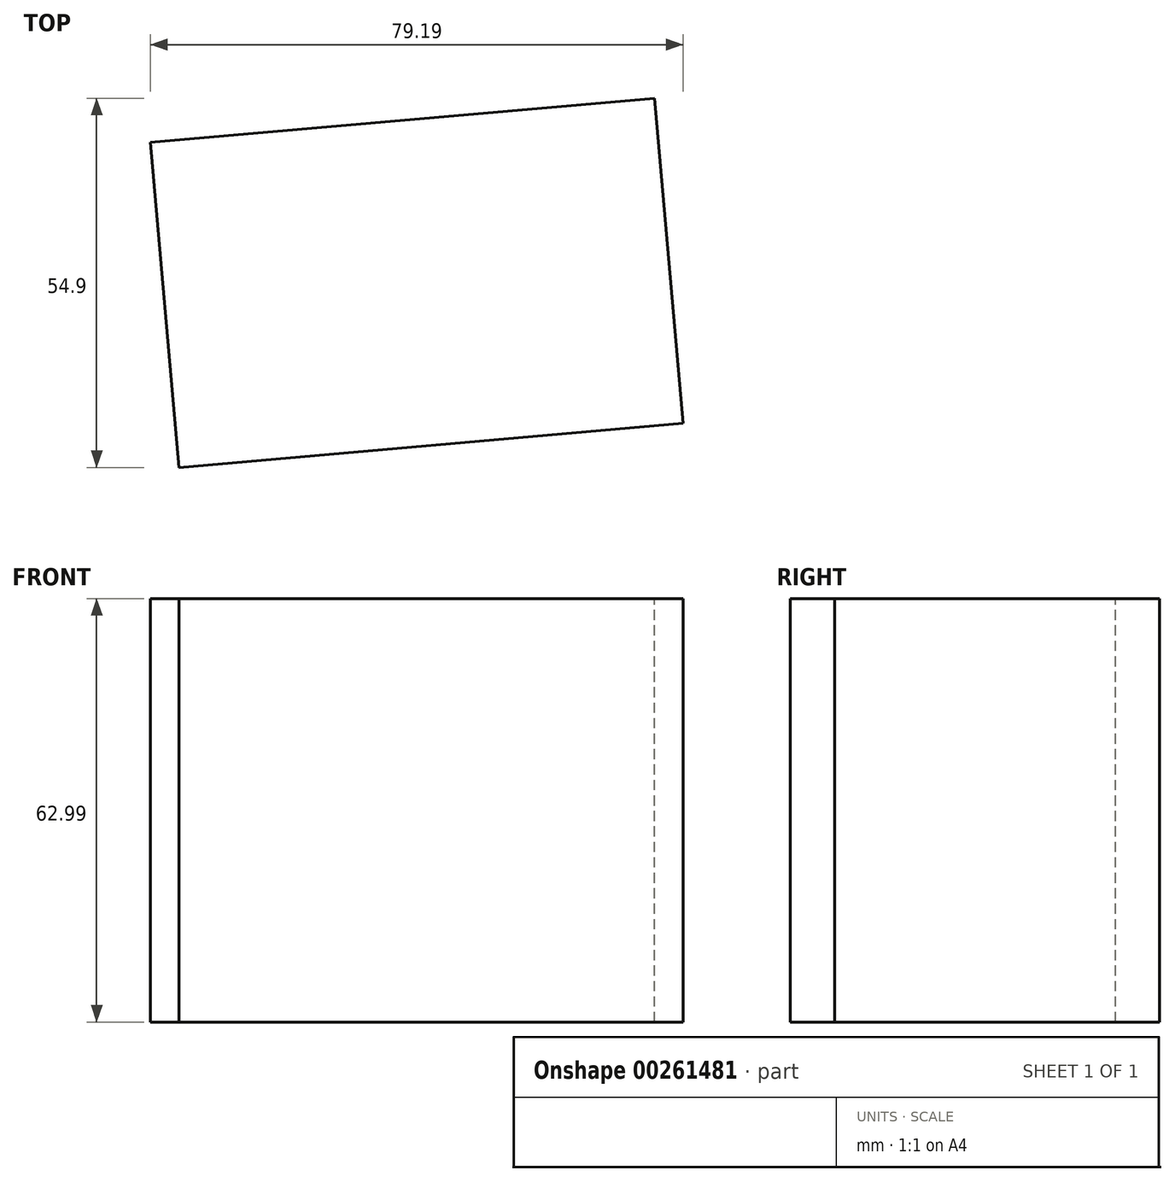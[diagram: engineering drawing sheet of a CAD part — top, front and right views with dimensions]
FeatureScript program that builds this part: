
annotation { "Feature Type Name" : "Feature", "Feature Type Description" : "" }
export const myFeature = defineFeature(function(context is Context, id is Id, definition is map)
    precondition{}
    {
        {
            var Q0;
            Q0=qCreatedBy(makeId("Top.planeOp"),FACE);
            var sketch = newSketch(context, id + "F0", { "sketchPlane" : qUnion([Q0])});
            skLineSegment(sketch, "E0.bottom", {"start": v(-41.34, -12.73) * mm, "end": v(33.91, -12.73) * mm});
            skLineSegment(sketch, "E0.top", {"start": v(-41.34, 35.8) * mm, "end": v(33.91, 35.8) * mm});
            skLineSegment(sketch, "E0.left", {"start": v(-41.34, -12.73) * mm, "end": v(-41.34, 35.8) * mm});
            skLineSegment(sketch, "E0.right", {"start": v(33.91, -12.73) * mm, "end": v(33.91, 35.8) * mm});
            skSolve(sketch);
        }
        {
            var Q0;
            Q0 = qSketchRegion(id + "F0", true);
            extrude(context, id + "F1", {"entities" : qUnion([Q0]), "depth" : 63 * mm});
        }
        {
            var Q0;
            Q0=makeQuery(id+"F1.opExtrude","SWEPT_BODY",BODY,{"disambiguationData":[OSD([sQuery(id+"F0.wireOp",EDGE,"E0.bottom"),sQuery(id+"F0.wireOp",EDGE,"E0.top"),sQuery(id+"F0.wireOp",EDGE,"E0.left"),sQuery(id+"F0.wireOp",EDGE,"E0.right")])]});
            var Q1;
            Q1=makeQuery(id+"F1.opExtrude","SWEPT_EDGE",EDGE,{"disambiguationData":[OSD([sQuery(id+"F0.wireOp",EDGE,"E0.top"),sQuery(id+"F0.wireOp",EDGE,"E0.right")])]});
            transform(context, id + "F2", {"entities" : qUnion([Q0]), "transformType" : TransformType.ROTATION, "transformAxis" : qUnion([Q1]), "angle" : 175 * degree, "makeCopy" : false});
        }
        {
            var Q0;
            Q0=makeQuery(id+"F1.opExtrude","SWEPT_BODY",BODY,{"disambiguationData":[OSD([sQuery(id+"F0.wireOp",EDGE,"E0.bottom"),sQuery(id+"F0.wireOp",EDGE,"E0.top"),sQuery(id+"F0.wireOp",EDGE,"E0.left"),sQuery(id+"F0.wireOp",EDGE,"E0.right")])]});
            var Q1;
            Q1=makeQuery(id+"F1.opExtrude","CAP_EDGE",EDGE,{"disambiguationData":[OSD([sQuery(id+"F0.wireOp",EDGE,"E0.right")])],"isStart":true});
            transform(context, id + "F3", {"entities" : qUnion([Q0]), "transformType" : TransformType.ROTATION, "transformAxis" : qUnion([Q1]), "angle" : 180 * degree, "oppositeDirection" : true, "makeCopy" : false});
        }
    });
